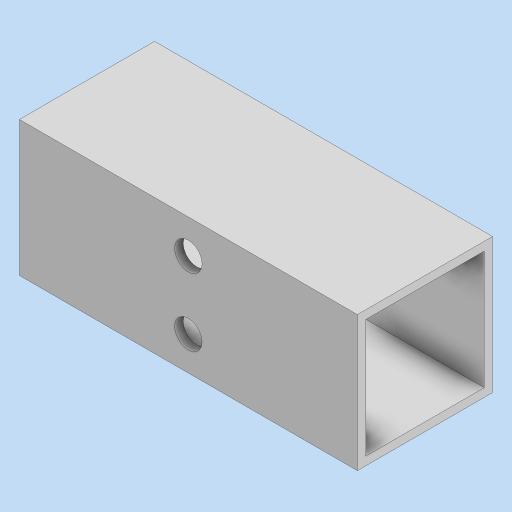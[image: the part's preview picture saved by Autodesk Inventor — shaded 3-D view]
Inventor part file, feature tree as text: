
AUTODESK INVENTOR PART (.ipt)
format: ipt  version: 2024 (Build 280153000, 153)  size: 116,224 bytes
history: native  units: in
note: dims shown in document units (in); Inventor stores cm internally (conversion verified against a paired STEP export)
features: extrude x2, sketch x2
ambient origin geometry x8: Origin, YZ Plane, XZ Plane, XY Plane, X Axis, Y Axis, Z Axis, Center Point
bodies: Solid1 (feature_tree)
feature tree (4):
  extrude  "Extrusion1"  Depth=1.0in
  extrude  "Extrusion2"  Depth=2.5in TaperAngle=0.0deg
  sketch  "Sketch1"  dims[d0=1.0in d1=1.0in]
  sketch  "Sketch2"  dims[d2=0.0625in d3=2.5in d4=0.0in d6=0.203in d7=0.203in d8=0.25in d9=0.25in d10=1.25in d11=1.25in d12=0.0in d13=0.0in]
